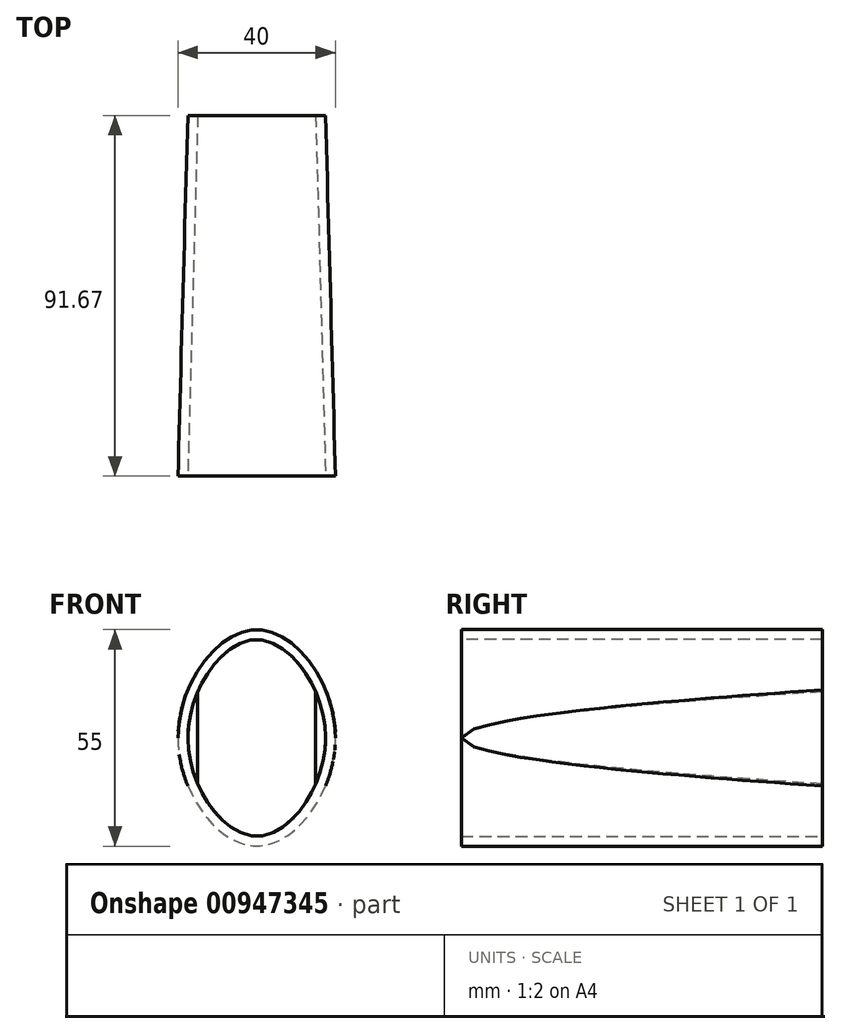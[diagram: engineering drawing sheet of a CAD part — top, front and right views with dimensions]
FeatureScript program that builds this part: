
annotation { "Feature Type Name" : "Feature", "Feature Type Description" : "" }
export const myFeature = defineFeature(function(context is Context, id is Id, definition is map)
    precondition{}
    {
        {
            var Q0;
            Q0=qCreatedBy(makeId("Top.planeOp"),FACE);
            var sketch = newSketch(context, id + "F0", { "sketchPlane" : qUnion([Q0])});
            skLineSegment(sketch, "E0", {"start": v(-14.55, 48) * mm, "end": v(-17.05, -43.66) * mm});
            skLineSegment(sketch, "E1", {"start": v(-17.05, -43.66) * mm, "end": v(22.95, -43.66) * mm});
            skLineSegment(sketch, "E2", {"start": v(22.95, -43.66) * mm, "end": v(20.45, 48) * mm});
            skLineSegment(sketch, "E3", {"start": v(20.45, 48) * mm, "end": v(-14.55, 48) * mm});
            skLineSegment(sketch, "E4", {"start": v(2.95, 48) * mm, "end": v(2.95, -43.66) * mm});
            skSolve(sketch);
        }
        {
            var Q0;
            Q0 = qSketchRegion(id + "F0", true);
            extrude(context, id + "F1", {"entities" : qUnion([Q0]), "depth" : 55 * mm, "offsetDistance" : 25 * mm});
        }
        {
            var Q0;
            Q0=makeQuery(id+"F1.opExtrude","SWEPT_FACE",FACE,{"disambiguationData":[OSD([sQuery(id+"F0.wireOp",EDGE,"E1")])]});
            var sketch = newSketch(context, id + "F2", { "sketchPlane" : qUnion([Q0])});
            skFitSpline(sketch, "E5", {"points": [v(2.95, 55) * mm, v(-17.05, 27.5) * mm, v(2.95, 0) * mm, v(22.95, 27.5) * mm, v(2.95, 55) * mm]});
            skSolve(sketch);
        }
        {
            var Q0;
            {var subQ0=sQuery(id+"F2.wireOp",EDGE,"E5");var subQ1=sQuery(id+"F0.wireOp",EDGE,"E1");var subQ4=makeQuery(id+"F1.opExtrude","CAP_EDGE",EDGE,{"disambiguationData":[OSD([subQ1])],"isStart":false});var subQ5=makeQuery(id+"F2.imprint","INTERSECT",VERTEX,{"derivedFrom":[subQ4,subQ0]});Q0=makeQuery(id+"F2.imprint","IMPRINT",FACE,{"disambiguationData":[TD([[makeQuery(id+"F2.imprint","IMPRINT",EDGE,{"disambiguationData":[TD([[subQ5,-1.0]])],"derivedFrom":subQ0}),-1.0]])]});}
            var Q1;
            {var subQ0=sQuery(id+"F2.wireOp",EDGE,"E5");var subQ1=sQuery(id+"F0.wireOp",EDGE,"E1");var subQ2=makeQuery(id+"F1.opExtrude","CAP_EDGE",EDGE,{"disambiguationData":[OSD([subQ1])],"isStart":false});var subQ3=makeQuery(id+"F2.imprint","INTERSECT",VERTEX,{"derivedFrom":[subQ2,subQ0]});Q1=makeQuery(id+"F2.imprint","IMPRINT",FACE,{"disambiguationData":[TD([[makeQuery(id+"F2.imprint","IMPRINT",EDGE,{"disambiguationData":[TD([[subQ3,1.0]])],"derivedFrom":subQ0}),-1.0]])]});}
            var Q2;
            {var subQ0=sQuery(id+"F2.wireOp",EDGE,"E5");var subQ1=sQuery(id+"F0.wireOp",EDGE,"E1");var subQ2=makeQuery(id+"F1.opExtrude","CAP_EDGE",EDGE,{"disambiguationData":[OSD([subQ1])],"isStart":true});var subQ3=makeQuery(id+"F2.imprint","INTERSECT",VERTEX,{"derivedFrom":[subQ2,subQ0]});Q2=makeQuery(id+"F2.imprint","IMPRINT",FACE,{"disambiguationData":[TD([[makeQuery(id+"F2.imprint","IMPRINT",EDGE,{"disambiguationData":[TD([[subQ3,-1.0]])],"derivedFrom":subQ0}),-1.0]])]});}
            var Q3;
            {var subQ0=sQuery(id+"F2.wireOp",EDGE,"E5");var subQ1=sQuery(id+"F0.wireOp",EDGE,"E1");var subQ4=makeQuery(id+"F1.opExtrude","CAP_EDGE",EDGE,{"disambiguationData":[OSD([subQ1])],"isStart":true});var subQ5=makeQuery(id+"F2.imprint","INTERSECT",VERTEX,{"derivedFrom":[subQ4,subQ0]});Q3=makeQuery(id+"F2.imprint","IMPRINT",FACE,{"disambiguationData":[TD([[makeQuery(id+"F2.imprint","IMPRINT",EDGE,{"disambiguationData":[TD([[subQ5,1.0]])],"derivedFrom":subQ0}),-1.0]])]});}
            extrude(context, id + "F3", {"entities" : qUnion([Q0, Q1, Q2, Q3]), "operationType" : NewBodyOperationType.REMOVE, "endBound" : BoundingType.THROUGH_ALL, "oppositeDirection" : true, "depth" : 25 * mm, "offsetDistance" : 25 * mm});
        }
        {
            var Q0;
            Q0=makeQuery(id+"F1.opExtrude","SWEPT_FACE",FACE,{"disambiguationData":[OSD([sQuery(id+"F0.wireOp",EDGE,"E1")])]});
            var Q1;
            Q1=makeQuery(id+"F1.opExtrude","SWEPT_FACE",FACE,{"disambiguationData":[OSD([sQuery(id+"F0.wireOp",EDGE,"E3")])]});
            shell(context, id + "F4", {"entities" : qUnion([Q0, Q1]), "thickness" : 2.5 * mm});
        }
    });
